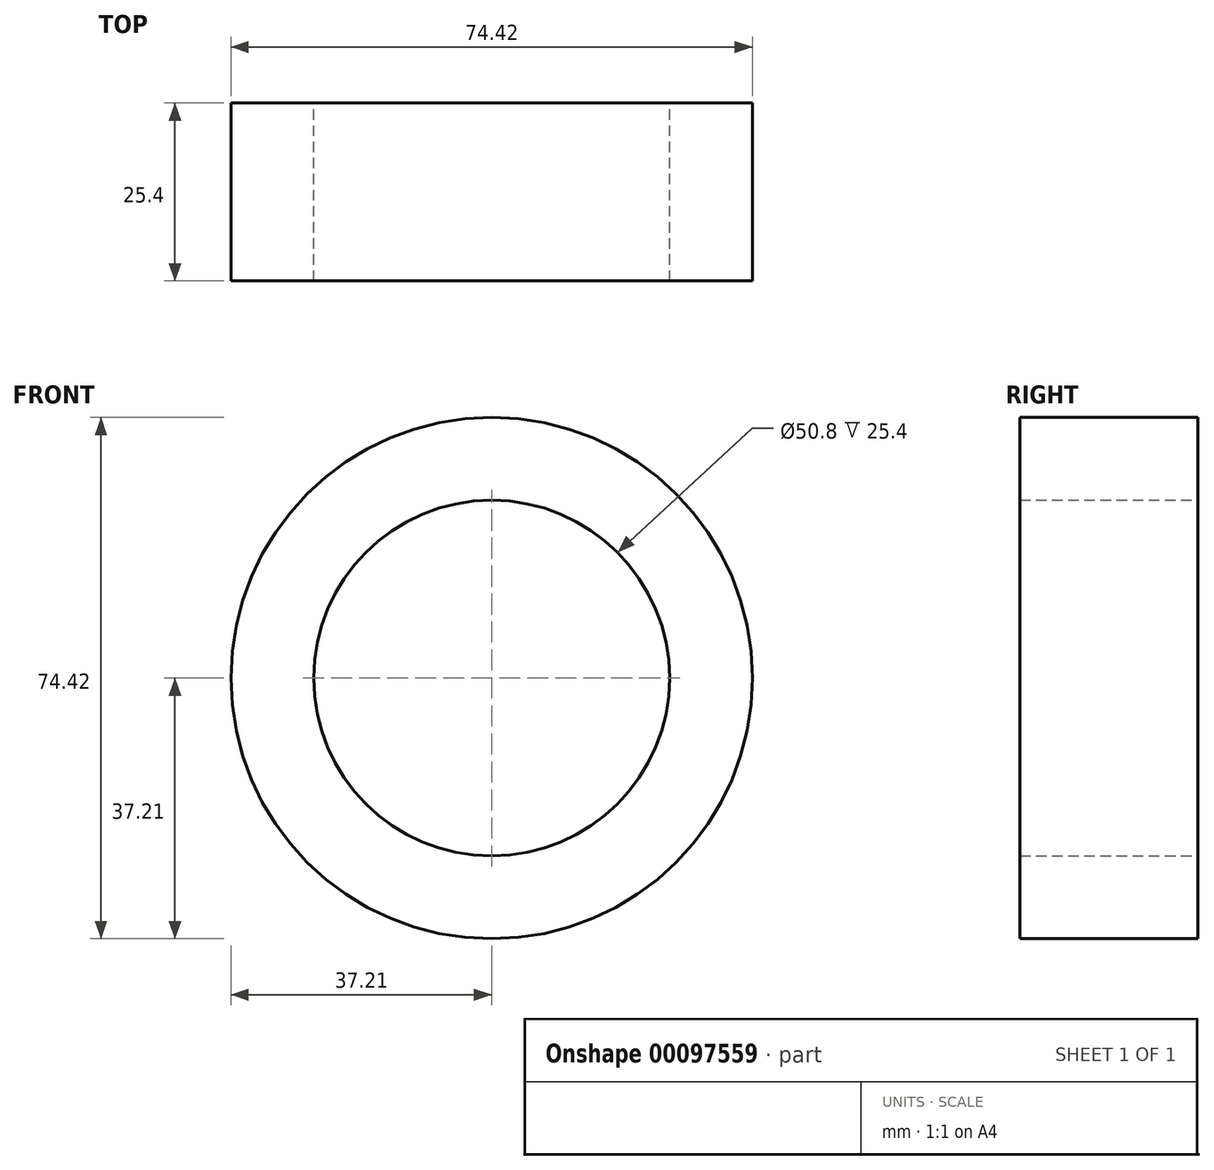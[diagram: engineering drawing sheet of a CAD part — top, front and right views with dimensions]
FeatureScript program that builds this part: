
annotation { "Feature Type Name" : "Feature", "Feature Type Description" : "" }
export const myFeature = defineFeature(function(context is Context, id is Id, definition is map)
    precondition{}
    {
        {
            var Q0;
            Q0=qCreatedBy(makeId("Front.planeOp"),FACE);
            var sketch = newSketch(context, id + "F0", { "sketchPlane" : qUnion([Q0])});
            skCircle(sketch, "E0", {"center": v(0, 0) * mm, "radius": 37.21 * mm});
            skSolve(sketch);
        }
        {
            var Q0;
            Q0 = qSketchRegion(id + "F0", true);
            extrude(context, id + "F1", {"entities" : qUnion([Q0]), "depth" : 25.4 * mm});
        }
        {
            var Q0;
            Q0=qCreatedBy(makeId("Front.planeOp"),FACE);
            var sketch = newSketch(context, id + "F2", { "sketchPlane" : qUnion([Q0])});
            skCircle(sketch, "E1", {"center": v(0, 0) * mm, "radius": 28.55 * mm});
            skSolve(sketch);
        }
        {
            var Q0;
            Q0=sQuery(id+"F2.wireOp",VERTEX,"E1.center");
            var Q1;
            Q1=makeQuery(id+"F1.opExtrude","SWEPT_BODY",BODY,{"disambiguationData":[OSD([sQuery(id+"F0.wireOp",EDGE,"E0")])]});
            hole(context, id + "F3", {"style" : HoleStyle.SIMPLE, "endStyle" : HoleEndStyle.THROUGH, "oppositeDirection" : true, "holeDiameter" : 50.8 * mm, "locations" : qUnion([Q0]), "scope" : qUnion([Q1]), "isTappedThrough" : true});
        }
    });
